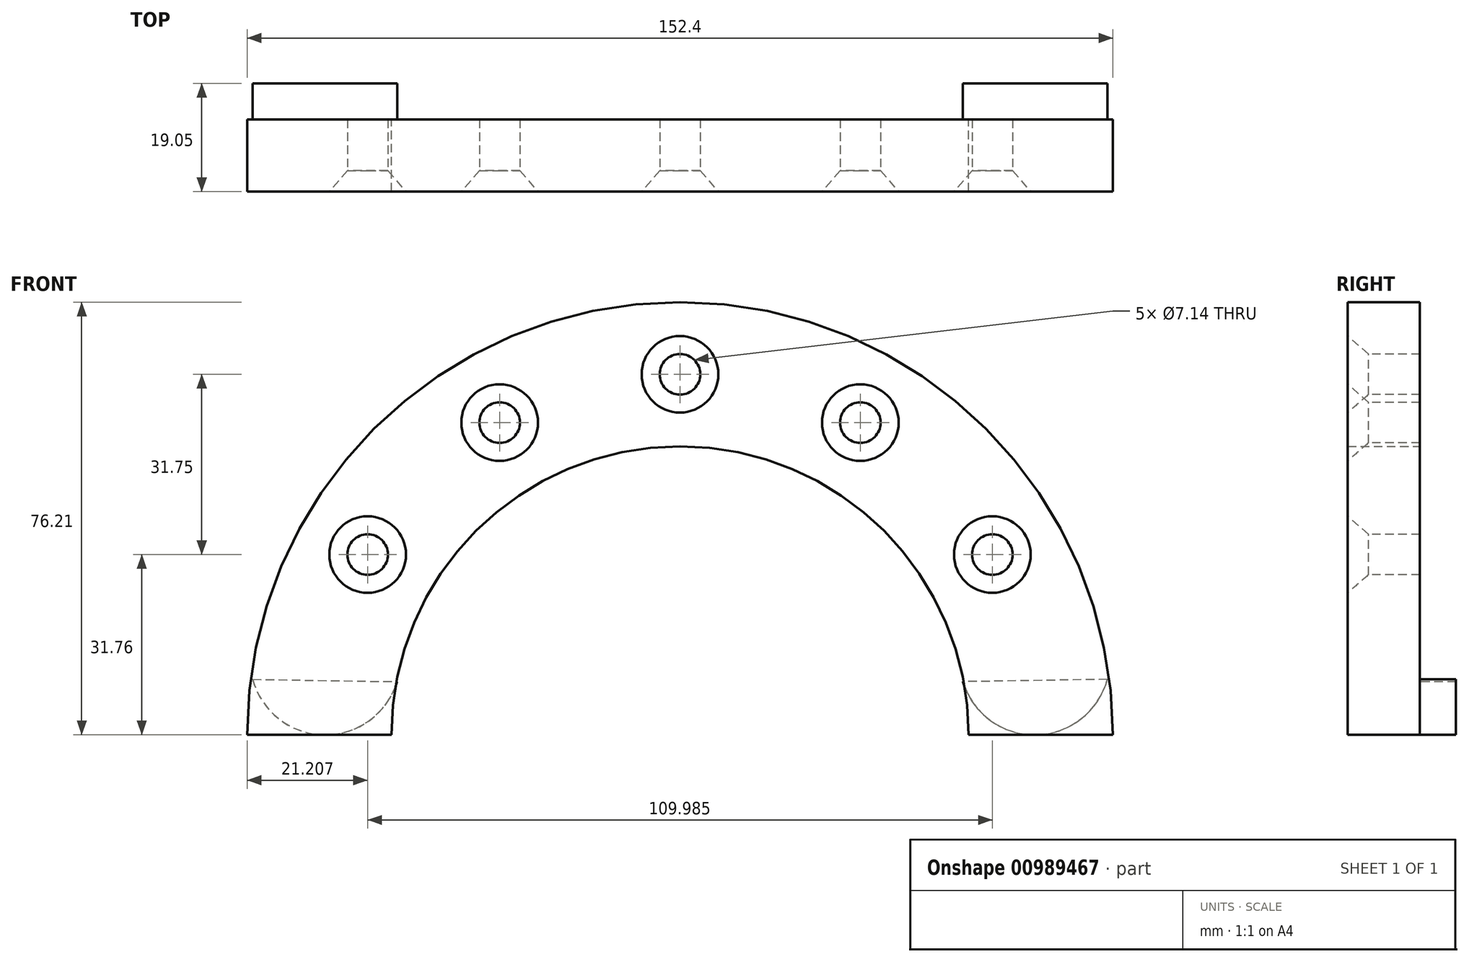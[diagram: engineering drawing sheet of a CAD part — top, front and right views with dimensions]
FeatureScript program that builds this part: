
annotation { "Feature Type Name" : "Feature", "Feature Type Description" : "" }
export const myFeature = defineFeature(function(context is Context, id is Id, definition is map)
    precondition{}
    {
        {
            var Q0;
            Q0=qCreatedBy(makeId("Front.planeOp"),FACE);
            var sketch = newSketch(context, id + "F0", { "sketchPlane" : qUnion([Q0])});
            skArc(sketch, "E0", {"start": v(76.2, 0) * mm, "mid": v(0, 76.2) * mm, "end": v(-76.2, 0) * mm});
            skArc(sketch, "E1", {"start": v(50.8, 0) * mm, "mid": v(0, 50.8) * mm, "end": v(-50.8, 0) * mm});
            skLineSegment(sketch, "E2", {"start": v(-76.2, 0) * mm, "end": v(-50.8, 0) * mm});
            skLineSegment(sketch, "E3", {"start": v(50.8, 0) * mm, "end": v(76.2, 0) * mm});
            skSolve(sketch);
        }
        {
            var Q0;
            Q0 = qSketchRegion(id + "F0", true);
            extrude(context, id + "F1", {"entities" : qUnion([Q0]), "depth" : 12.7 * mm, "offsetDistance" : 25.4 * mm});
        }
        {
            var Q0;
            Q0=qCreatedBy(makeId("Front.planeOp"),FACE);
            var sketch = newSketch(context, id + "F2", { "sketchPlane" : qUnion([Q0])});
            skArc(sketch, "E4", {"start": v(49.8, 9.35) * mm, "mid": v(62.67, -0.01) * mm, "end": v(75.24, 9.76) * mm});
            skLineSegment(sketch, "E5", {"start": v(75.24, 9.76) * mm, "end": v(49.8, 9.35) * mm});
            skLineSegment(sketch, "E6", {"start": v(0, 0) * mm, "end": v(0, 98.3) * mm, "construction": true});
            skLineSegment(sketch, "E7.MirrorCS", {"start": v(-75.24, 9.76) * mm, "end": v(-49.8, 9.35) * mm});
            skArc(sketch, "E8.MirrorCS", {"start": v(-49.8, 9.35) * mm, "mid": v(-62.67, -0.01) * mm, "end": v(-75.24, 9.76) * mm});
            skSolve(sketch);
        }
        {
            var Q0;
            Q0 = qSketchRegion(id + "F2", true);
            extrude(context, id + "F3", {"entities" : qUnion([Q0]), "operationType" : NewBodyOperationType.ADD, "oppositeDirection" : true, "depth" : 6.35 * mm, "offsetDistance" : 25.4 * mm});
        }
        {
            var Q0;
            Q0=makeQuery(id+"F1.opExtrude","CAP_FACE",FACE,{"disambiguationData":[OSD([sQuery(id+"F0.wireOp",EDGE,"E0"),sQuery(id+"F0.wireOp",EDGE,"E1"),sQuery(id+"F0.wireOp",EDGE,"E2"),sQuery(id+"F0.wireOp",EDGE,"E3")])],"isStart":false});
            var sketch = newSketch(context, id + "F4", { "sketchPlane" : qUnion([Q0])});
            skArc(sketch, "E9", {"start": v(63.5, 0) * mm, "mid": v(0, 63.5) * mm, "end": v(-63.5, 0) * mm, "construction": true});
            skPoint(sketch, "E10", {"position": v(-63.5, 0) * mm});
            skPoint(sketch, "E11.1.0", {"position": v(-55, 31.75) * mm});
            skPoint(sketch, "E11.2.0", {"position": v(-31.75, 55) * mm});
            skPoint(sketch, "E11.3.0", {"position": v(0, 63.5) * mm});
            skPoint(sketch, "E11.4.0", {"position": v(31.75, 55) * mm});
            skPoint(sketch, "E11.5.0", {"position": v(55, 31.75) * mm});
            skPoint(sketch, "E11.6.0", {"position": v(63.5, 0) * mm});
            skLineSegment(sketch, "E11.anchor1", {"start": v(0, 0) * mm, "end": v(-63.5, 0) * mm, "construction": true});
            skLineSegment(sketch, "E11.anchor2", {"start": v(0, 0) * mm, "end": v(63.5, 0) * mm, "construction": true});
            skSolve(sketch);
        }
        {
            var Q0;
            Q0=sQuery(id+"F4.wireOp",VERTEX,"E11.1.0");
            var Q1;
            Q1=sQuery(id+"F4.wireOp",VERTEX,"E11.2.0");
            var Q2;
            Q2=sQuery(id+"F4.wireOp",VERTEX,"E11.3.0");
            var Q3;
            Q3=sQuery(id+"F4.wireOp",VERTEX,"E11.4.0");
            var Q4;
            Q4=sQuery(id+"F4.wireOp",VERTEX,"E11.5.0");
            var Q5;
            Q5=makeQuery(id+"F1.opExtrude","SWEPT_BODY",BODY,{"disambiguationData":[OSD([sQuery(id+"F0.wireOp",EDGE,"E0"),sQuery(id+"F0.wireOp",EDGE,"E1"),sQuery(id+"F0.wireOp",EDGE,"E2"),sQuery(id+"F0.wireOp",EDGE,"E3")])]});
            hole(context, id + "F5", {"style" : HoleStyle.C_SINK, "endStyle" : HoleEndStyle.THROUGH, "standardTappedOrClearance" : lookupTablePath({ "fit" : "Normal (ASME)", "standard" : "ANSI", "size" : "1/4", "type" : "Clearance" }), "standardBlindInLast" : lookupTablePath({ "fit" : "Normal", "standard" : "ANSI", "engagement" : "75%", "pitch" : "20 tpi", "size" : "1/4", "type" : "Clearance & tapped" }), "holeDiameter" : 7.14 * mm, "cSinkDiameter" : 13.5 * mm, "cSinkAngle" : 82 * degree, "majorDiameter" : 6.35 * mm, "isTappedThrough" : true, "tappedDepth" : 12.7 * mm, "tapClearance" : 3, "locations" : qUnion([Q0, Q1, Q2, Q3, Q4]), "scope" : qUnion([Q5])});
        }
    });
